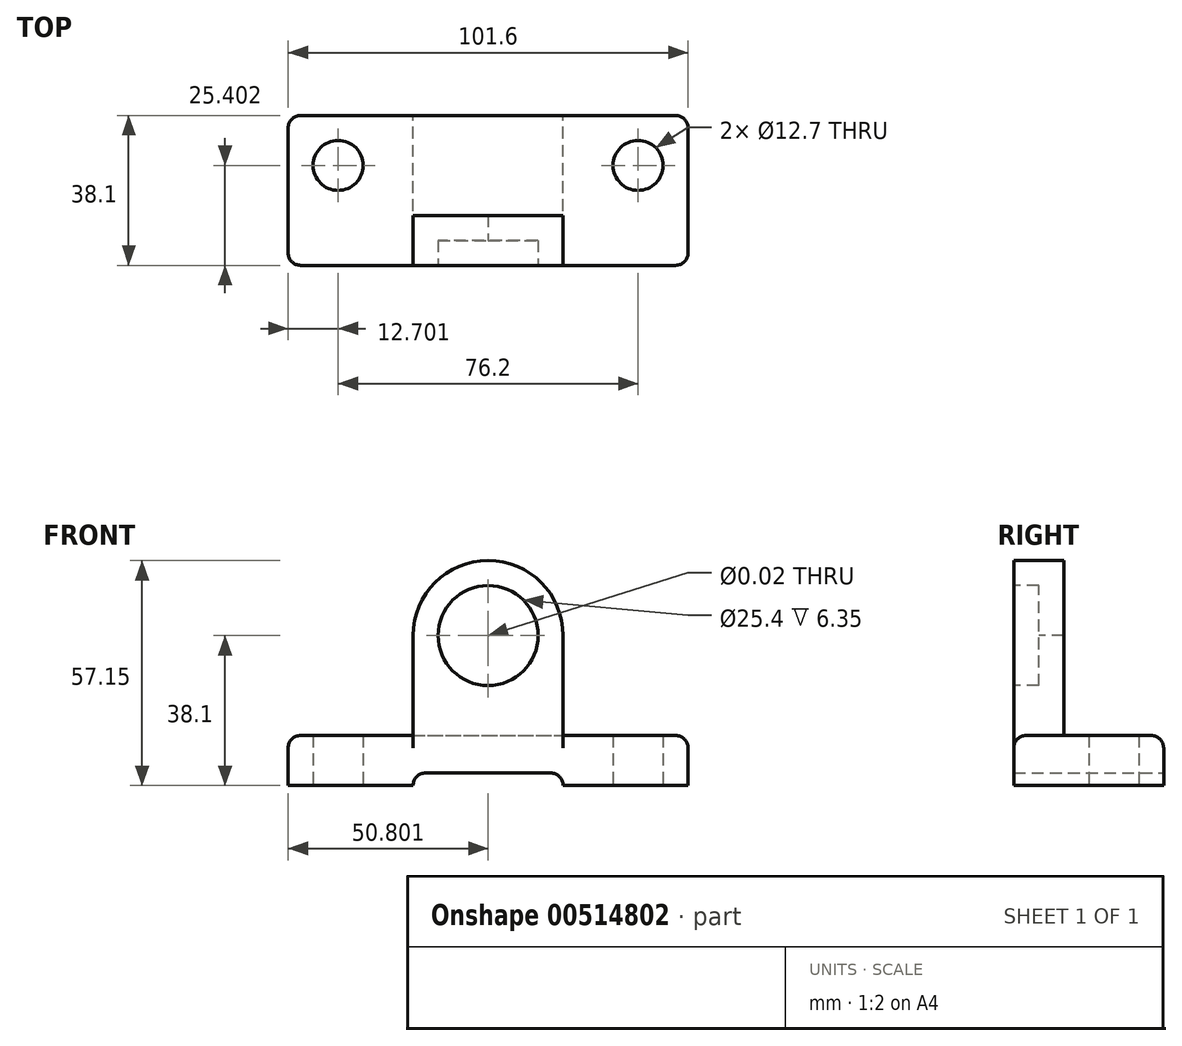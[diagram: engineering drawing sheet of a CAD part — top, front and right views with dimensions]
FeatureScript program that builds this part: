
annotation { "Feature Type Name" : "Feature", "Feature Type Description" : "" }
export const myFeature = defineFeature(function(context is Context, id is Id, definition is map)
    precondition{}
    {
        {
            var Q0;
            Q0=qCreatedBy(makeId("Top.planeOp"),FACE);
            var sketch = newSketch(context, id + "F0", { "sketchPlane" : qUnion([Q0])});
            skLineSegment(sketch, "E0.bottom", {"start": v(-38.44, 22.42) * mm, "end": v(63.16, 22.42) * mm});
            skLineSegment(sketch, "E0.top", {"start": v(-38.44, -15.68) * mm, "end": v(63.16, -15.68) * mm});
            skLineSegment(sketch, "E0.left", {"start": v(-38.44, 22.42) * mm, "end": v(-38.44, -15.68) * mm});
            skLineSegment(sketch, "E0.right", {"start": v(63.16, 22.42) * mm, "end": v(63.16, -15.68) * mm});
            skCircle(sketch, "E1", {"center": v(-25.74, 9.72) * mm, "radius": 6.35 * mm});
            skCircle(sketch, "E2", {"center": v(50.46, 9.72) * mm, "radius": 6.35 * mm});
            skSolve(sketch);
        }
        {
            var Q0;
            Q0 = qSketchRegion(id + "F0", true);
            extrude(context, id + "F1", {"entities" : qUnion([Q0]), "depth" : 12.7 * mm, "offsetDistance" : 25.4 * mm});
        }
        {
            var Q0;
            Q0=makeQuery(id+"F1.opExtrude","SWEPT_FACE",FACE,{"disambiguationData":[OSD([sQuery(id+"F0.wireOp",EDGE,"E0.top")])]});
            var sketch = newSketch(context, id + "F2", { "sketchPlane" : qUnion([Q0])});
            skLineSegment(sketch, "E3", {"start": v(-6.69, 0) * mm, "end": v(-6.69, 38.1) * mm});
            skArc(sketch, "E4", {"start": v(31.41, 38.1) * mm, "mid": v(12.36, 57.15) * mm, "end": v(-6.69, 38.1) * mm});
            skLineSegment(sketch, "E5", {"start": v(31.41, 38.1) * mm, "end": v(31.41, 0) * mm});
            skLineSegment(sketch, "E6", {"start": v(31.41, 0) * mm, "end": v(-6.69, 0) * mm});
            skSolve(sketch);
        }
        {
            var Q0;
            {var subQ0=sQuery(id+"F2.wireOp",EDGE,"E4");Q0=makeQuery(id+"F2.imprint","IMPRINT",FACE,{"disambiguationData":[TD([[makeQuery(id+"F2.imprint","IMPRINT",EDGE,{"derivedFrom":subQ0}),1.0]])]});}
            extrude(context, id + "F3", {"entities" : qUnion([Q0]), "oppositeDirection" : true, "depth" : 12.7 * mm, "offsetDistance" : 25.4 * mm});
        }
        {
            var Q0;
            Q0=sQuery(id+"F2.wireOp",VERTEX,"E4.center");
            var Q1;
            Q1=makeQuery(id+"F3.opExtrude","SWEPT_BODY",BODY,{"disambiguationData":[OSD([sQuery(id+"F0.wireOp",EDGE,"E0.top"),sQuery(id+"F2.wireOp",EDGE,"E3"),sQuery(id+"F2.wireOp",EDGE,"E4"),sQuery(id+"F2.wireOp",EDGE,"E5")])]});
            hole(context, id + "F4", {"style" : HoleStyle.C_BORE, "endStyle" : HoleEndStyle.THROUGH, "standardTappedOrClearance" : lookupTablePath({ "standard" : "ANSI", "size" : "15/32 (0.47)", "type" : "Drilled" }), "standardBlindInLast" : lookupTablePath({ "standard" : "ANSI", "size" : "15/32", "type" : "Drilled" }), "holeDiameter" : 15 / 812.8 * mm, "cBoreDiameter" : 25.4 * mm, "cBoreDepth" : 6.35 * mm, "isTappedThrough" : true, "tappedDepth" : 12.7 * mm, "tapClearance" : 3, "locations" : qUnion([Q0]), "scope" : qUnion([Q1])});
        }
        {
            var Q0;
            Q0=makeQuery(id+"F1.opExtrude","SWEPT_FACE",FACE,{"disambiguationData":[OSD([sQuery(id+"F0.wireOp",EDGE,"E0.bottom")])]});
            var sketch = newSketch(context, id + "F5", { "sketchPlane" : qUnion([Q0])});
            skLineSegment(sketch, "E7", {"start": v(-31.41, 0) * mm, "end": v(-31.41, 3.17) * mm});
            skLineSegment(sketch, "E8", {"start": v(-31.41, 3.17) * mm, "end": v(6.69, 3.17) * mm});
            skLineSegment(sketch, "E9", {"start": v(6.69, 3.17) * mm, "end": v(6.69, 0) * mm});
            skLineSegment(sketch, "E10", {"start": v(6.69, 0) * mm, "end": v(-31.41, 0) * mm});
            skSolve(sketch);
        }
        {
            var Q0;
            Q0 = qSketchRegion(id + "F5", true);
            extrude(context, id + "F6", {"entities" : qUnion([Q0]), "operationType" : NewBodyOperationType.REMOVE, "endBound" : BoundingType.THROUGH_ALL, "oppositeDirection" : true, "depth" : 25.4 * mm, "offsetDistance" : 25.4 * mm});
        }
        {
            var Q0;
            Q0=sQuery(id+"F0.wireOp",VERTEX,"E1.center");
            var Q1;
            Q1=makeQuery(id+"F1.opExtrude","SWEPT_BODY",BODY,{"disambiguationData":[OSD([sQuery(id+"F0.wireOp",EDGE,"E0.bottom"),sQuery(id+"F0.wireOp",EDGE,"E0.top"),sQuery(id+"F0.wireOp",EDGE,"E0.left"),sQuery(id+"F0.wireOp",EDGE,"E0.right"),sQuery(id+"F0.wireOp",EDGE,"E1"),sQuery(id+"F0.wireOp",EDGE,"E2")])]});
            hole(context, id + "F7", {"style" : HoleStyle.SIMPLE, "endStyle" : HoleEndStyle.THROUGH, "oppositeDirection" : true, "standardTappedOrClearance" : lookupTablePath({ "standard" : "ANSI", "fit" : "Normal (ASME)", "size" : "3/8", "type" : "Clearance" }), "standardBlindInLast" : lookupTablePath({ "fit" : "Free", "standard" : "ANSI", "size" : "3/8", "type" : "Clearance" }), "holeDiameter" : 10.08 * mm, "isTappedThrough" : true, "tappedDepth" : 12.7 * mm, "tapClearance" : 3, "locations" : qUnion([Q0]), "scope" : qUnion([Q1])});
        }
        {
            var Q0;
            Q0=makeQuery(id+"F1.opExtrude","SWEPT_BODY",BODY,{"disambiguationData":[OSD([sQuery(id+"F0.wireOp",EDGE,"E0.bottom"),sQuery(id+"F0.wireOp",EDGE,"E0.top"),sQuery(id+"F0.wireOp",EDGE,"E0.left"),sQuery(id+"F0.wireOp",EDGE,"E0.right"),sQuery(id+"F0.wireOp",EDGE,"E1"),sQuery(id+"F0.wireOp",EDGE,"E2")])]});
            var Q1;
            Q1=makeQuery(id+"F3.opExtrude","SWEPT_BODY",BODY,{"disambiguationData":[OSD([sQuery(id+"F0.wireOp",EDGE,"E0.top"),sQuery(id+"F2.wireOp",EDGE,"E3"),sQuery(id+"F2.wireOp",EDGE,"E4"),sQuery(id+"F2.wireOp",EDGE,"E5")])]});
            booleanBodies(context, id + "F8", {"operationType" : BooleanOperationType.UNION, "tools" : qUnion([Q0, Q1])});
        }
        {
            var Q0;
            Q0=makeQuery(id+"F1.opExtrude","SWEPT_EDGE",EDGE,{"disambiguationData":[OSD([sQuery(id+"F0.wireOp",EDGE,"E0.top"),sQuery(id+"F0.wireOp",EDGE,"E0.right")])]});
            var Q1;
            Q1=makeQuery(id+"F1.opExtrude","SWEPT_EDGE",EDGE,{"disambiguationData":[OSD([sQuery(id+"F0.wireOp",EDGE,"E0.bottom"),sQuery(id+"F0.wireOp",EDGE,"E0.right")])]});
            var Q2;
            Q2=makeQuery(id+"F1.opExtrude","SWEPT_EDGE",EDGE,{"disambiguationData":[OSD([sQuery(id+"F0.wireOp",EDGE,"E0.top"),sQuery(id+"F0.wireOp",EDGE,"E0.left")])]});
            var Q3;
            Q3=makeQuery(id+"F1.opExtrude","SWEPT_EDGE",EDGE,{"disambiguationData":[OSD([sQuery(id+"F0.wireOp",EDGE,"E0.bottom"),sQuery(id+"F0.wireOp",EDGE,"E0.left")])]});
            var Q4;
            Q4=makeQuery(id+"F6.boolean.opBoolean","COPY",EDGE,{"derivedFrom":makeQuery(id+"F6.opExtrude","SWEPT_EDGE",EDGE,{"disambiguationData":[OSD([sQuery(id+"F5.wireOp",EDGE,"E8"),sQuery(id+"F5.wireOp",EDGE,"E9")])]})});
            var Q5;
            Q5=makeQuery(id+"F6.boolean.opBoolean","COPY",EDGE,{"derivedFrom":makeQuery(id+"F6.opExtrude","SWEPT_EDGE",EDGE,{"disambiguationData":[OSD([sQuery(id+"F5.wireOp",EDGE,"E7"),sQuery(id+"F5.wireOp",EDGE,"E8")])]})});
            var Q6;
            Q6=makeQuery(id+"F1.opExtrude","CAP_EDGE",EDGE,{"disambiguationData":[OSD([sQuery(id+"F0.wireOp",EDGE,"E0.bottom")])],"isStart":false});
            var Q7;
            Q7=makeQuery(id+"F1.opExtrude","CAP_EDGE",EDGE,{"disambiguationData":[OSD([sQuery(id+"F0.wireOp",EDGE,"E0.right")])],"isStart":false});
            var Q8;
            Q8=makeQuery(id+"F1.opExtrude","CAP_EDGE",EDGE,{"disambiguationData":[OSD([sQuery(id+"F0.wireOp",EDGE,"E0.left")])],"isStart":false});
            var Q9;
            {var subQ1=sQuery(id+"F0.wireOp",EDGE,"E0.top");var subQ2=sQuery(id+"F0.wireOp",EDGE,"E0.right");Q9=makeQuery(id+"F8.opBoolean","SPLIT",EDGE,{"disambiguationData":[TD([makeQuery(id+"F1.opExtrude","SWEPT_FACE",FACE,{"disambiguationData":[OSD([subQ2])]})])],"derivedFrom":makeQuery(id+"F1.opExtrude","CAP_EDGE",EDGE,{"disambiguationData":[OSD([subQ1])],"isStart":false})});}
            var Q10;
            {var subQ0=sQuery(id+"F0.wireOp",EDGE,"E0.left");var subQ2=sQuery(id+"F0.wireOp",EDGE,"E0.top");Q10=makeQuery(id+"F8.opBoolean","SPLIT",EDGE,{"disambiguationData":[TD([makeQuery(id+"F1.opExtrude","SWEPT_FACE",FACE,{"disambiguationData":[OSD([subQ0])]})])],"derivedFrom":makeQuery(id+"F1.opExtrude","CAP_EDGE",EDGE,{"disambiguationData":[OSD([subQ2])],"isStart":false})});}
            var Q11;
            Q11=makeQuery(id+"F3.opExtrude","CAP_EDGE",EDGE,{"disambiguationData":[OSD([sQuery(id+"F0.wireOp",EDGE,"E0.top")])],"isStart":false});
            var Q12;
            Q12=makeQuery(id+"F3.opExtrude","SWEPT_EDGE",EDGE,{"disambiguationData":[OSD([sQuery(id+"F0.wireOp",EDGE,"E0.top"),sQuery(id+"F2.wireOp",EDGE,"E5")])]});
            var Q13;
            Q13=makeQuery(id+"F3.opExtrude","SWEPT_EDGE",EDGE,{"disambiguationData":[OSD([sQuery(id+"F0.wireOp",EDGE,"E0.top"),sQuery(id+"F2.wireOp",EDGE,"E3")])]});
            fillet(context, id + "F9", {"entities" : qUnion([Q0, Q1, Q2, Q3, Q4, Q5, Q6, Q7, Q8, Q9, Q10, Q11, Q12, Q13]), "radius" : 3.17 * mm, "tangentPropagation" : true, "allowEdgeOverflow" : false});
        }
    });
